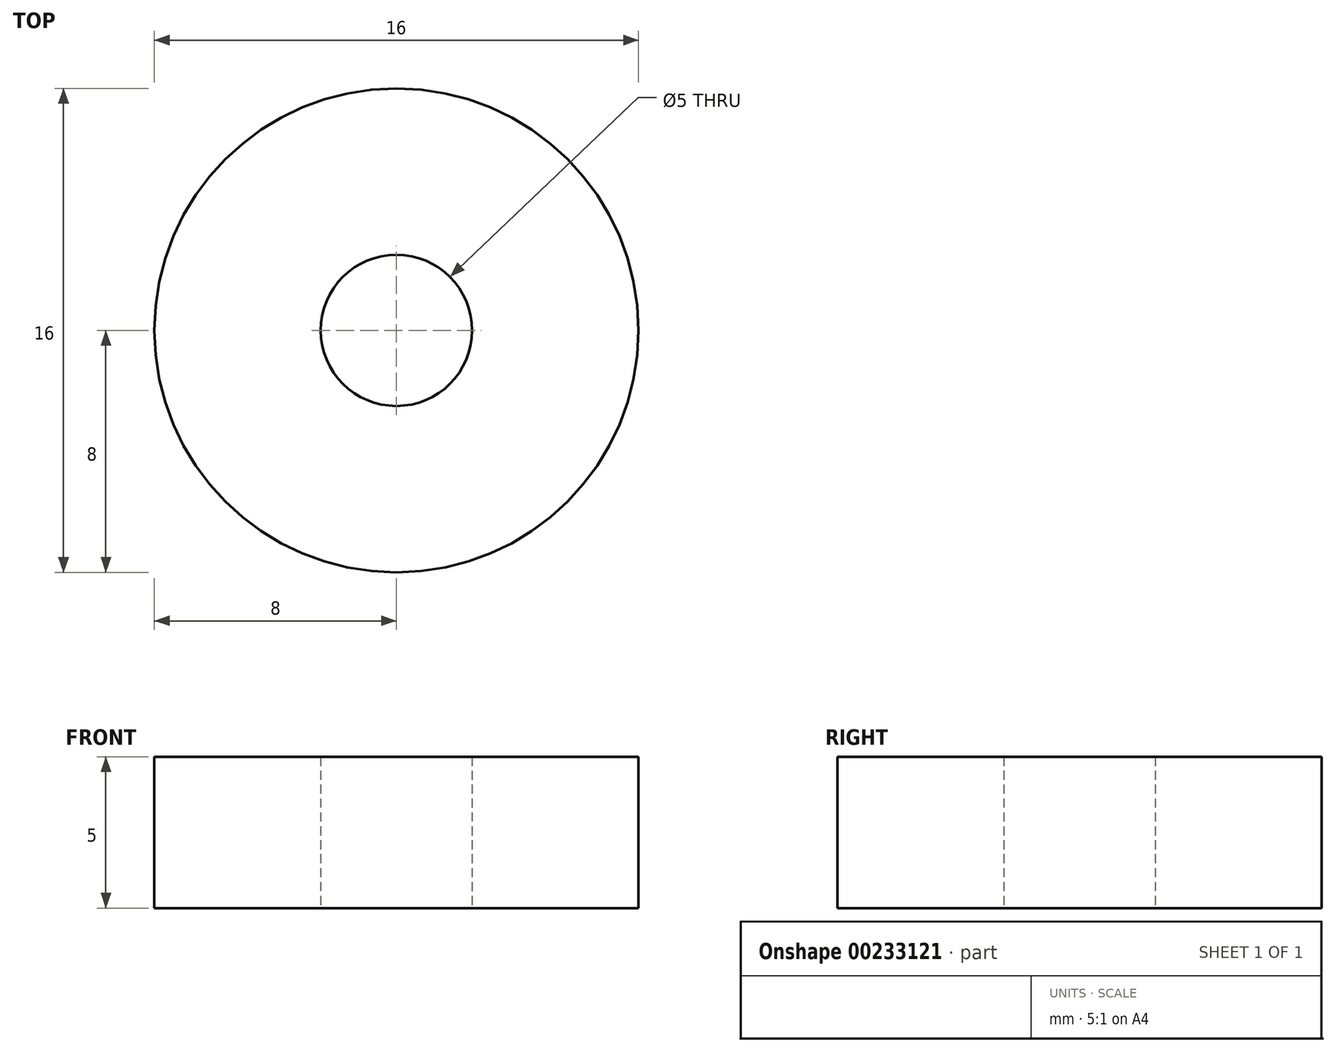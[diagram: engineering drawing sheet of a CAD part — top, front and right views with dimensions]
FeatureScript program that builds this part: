
annotation { "Feature Type Name" : "Feature", "Feature Type Description" : "" }
export const myFeature = defineFeature(function(context is Context, id is Id, definition is map)
    precondition{}
    {
        {
            var Q0;
            Q0=qCreatedBy(makeId("Top.planeOp"),FACE);
            var sketch = newSketch(context, id + "F0", { "sketchPlane" : qUnion([Q0])});
            skCircle(sketch, "E0", {"center": v(0, 0) * mm, "radius": 8 * mm});
            skCircle(sketch, "E1", {"center": v(0, 0) * mm, "radius": 2.5 * mm});
            skSolve(sketch);
        }
        {
            var Q0;
            Q0 = qSketchRegion(id + "F0", true);
            extrude(context, id + "F1", {"entities" : qUnion([Q0]), "depth" : 5 * mm, "symmetric" : true});
        }
    });
